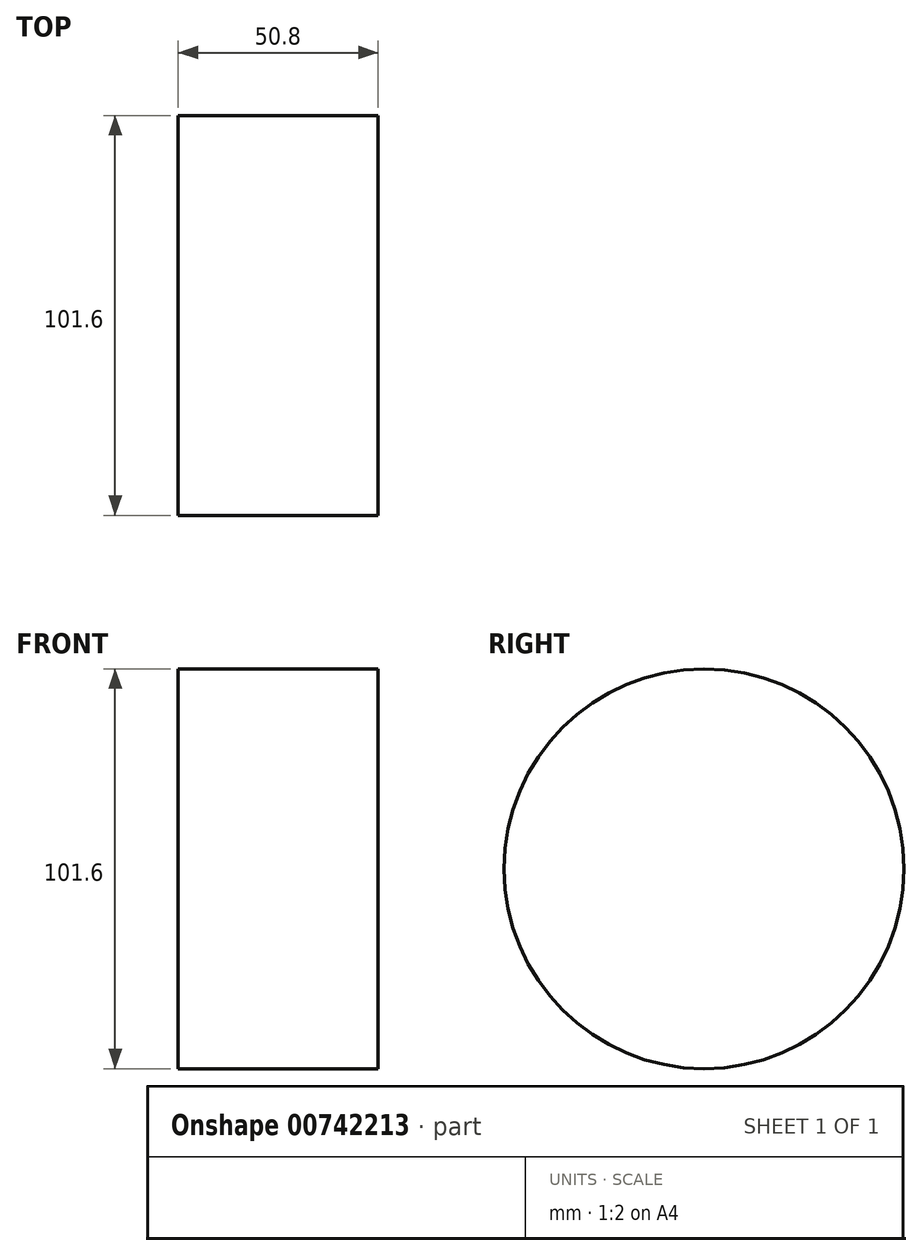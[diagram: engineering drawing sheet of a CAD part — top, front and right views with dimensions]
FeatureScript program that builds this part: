
annotation { "Feature Type Name" : "Feature", "Feature Type Description" : "" }
export const myFeature = defineFeature(function(context is Context, id is Id, definition is map)
    precondition{}
    {
        {
            var Q0;
            Q0=qCreatedBy(makeId("Right.planeOp"),FACE);
            var sketch = newSketch(context, id + "F0", { "sketchPlane" : qUnion([Q0])});
            skCircle(sketch, "E0", {"center": v(0, 0) * mm, "radius": 50.8 * mm});
            skSolve(sketch);
        }
        {
            var Q0;
            Q0=makeQuery(id+"F0.imprint","IMPRINT",FACE,{"disambiguationData":[TD([[makeQuery(id+"F0.imprint","IMPRINT",EDGE,{"derivedFrom":sQuery(id+"F0.wireOp",EDGE,"E0")}),1.0]])]});
            extrude(context, id + "F1", {"entities" : qUnion([Q0]), "depth" : 50.8 * mm, "offsetDistance" : 25.4 * mm});
        }
    });
